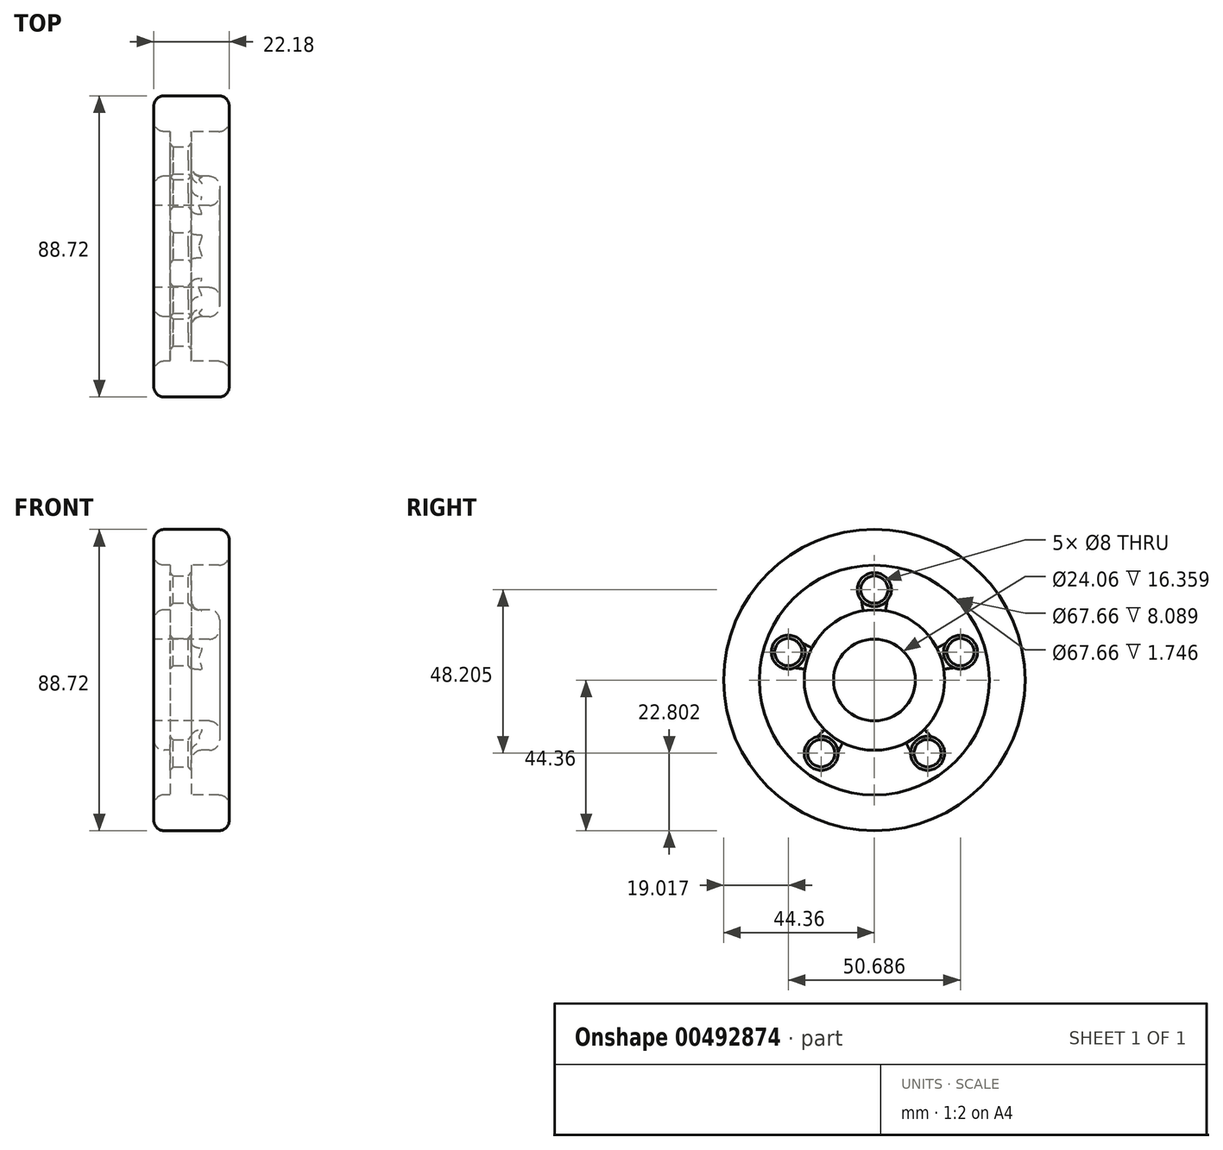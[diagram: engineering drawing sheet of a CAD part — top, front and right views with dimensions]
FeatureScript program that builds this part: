
annotation { "Feature Type Name" : "Feature", "Feature Type Description" : "" }
export const myFeature = defineFeature(function(context is Context, id is Id, definition is map)
    precondition{}
    {
        {
            var Q0;
            Q0=qCreatedBy(makeId("Front.planeOp"),FACE);
            var sketch = newSketch(context, id + "F0", { "sketchPlane" : qUnion([Q0])});
            skLineSegment(sketch, "E0", {"start": v(0, 12.03) * mm, "end": v(19.36, 12.03) * mm});
            skLineSegment(sketch, "E1", {"start": v(19.36, 12.03) * mm, "end": v(19.36, 20.67) * mm});
            skLineSegment(sketch, "E2", {"start": v(19.36, 20.67) * mm, "end": v(11.09, 20.67) * mm});
            skLineSegment(sketch, "E3", {"start": v(11.09, 20.67) * mm, "end": v(11.09, 33.83) * mm});
            skLineSegment(sketch, "E4", {"start": v(11.09, 33.83) * mm, "end": v(22.18, 33.83) * mm});
            skLineSegment(sketch, "E5", {"start": v(22.18, 33.83) * mm, "end": v(22.18, 44.36) * mm});
            skLineSegment(sketch, "E6", {"start": v(22.18, 44.36) * mm, "end": v(0, 44.36) * mm});
            skLineSegment(sketch, "E7", {"start": v(0, 44.36) * mm, "end": v(0, 33.83) * mm});
            skLineSegment(sketch, "E8", {"start": v(0, 33.83) * mm, "end": v(4.75, 33.83) * mm});
            skLineSegment(sketch, "E9", {"start": v(4.75, 33.83) * mm, "end": v(4.75, 20.67) * mm});
            skLineSegment(sketch, "E10", {"start": v(4.75, 20.67) * mm, "end": v(0, 20.67) * mm});
            skLineSegment(sketch, "E11", {"start": v(0, 20.67) * mm, "end": v(0, 12.03) * mm});
            skLineSegment(sketch, "E12", {"start": v(0, 0) * mm, "end": v(19.36, 0) * mm});
            skSolve(sketch);
        }
        {
            var Q0;
            Q0 = qSketchRegion(id + "F0", true);
            var Q1;
            Q1=sQuery(id+"F0.wireOp",EDGE,"E12");
            revolve(context, id + "F1", {"entities" : qUnion([Q0]), "axis" : qUnion([Q1]), "revolveType" : RevolveType.FULL});
        }
        {
            var Q0;
            Q0=makeQuery(id+"F1.opRevolve","SWEPT_FACE",FACE,{"disambiguationData":[OSD([sQuery(id+"F0.wireOp",EDGE,"E3")])]});
            var sketch = newSketch(context, id + "F2", { "sketchPlane" : qUnion([Q0])});
            skCircle(sketch, "E13", {"center": v(0, 26.65) * mm, "radius": 4 * mm});
            skCircle(sketch, "E14.1.0", {"center": v(-25.34, 8.23) * mm, "radius": 4 * mm});
            skCircle(sketch, "E14.2.0", {"center": v(-15.66, -21.56) * mm, "radius": 4 * mm});
            skCircle(sketch, "E14.3.0", {"center": v(15.66, -21.56) * mm, "radius": 4 * mm});
            skCircle(sketch, "E14.4.0", {"center": v(25.34, 8.23) * mm, "radius": 4 * mm});
            skPoint(sketch, "E14.center", {"position": v(0, 0) * mm});
            skSolve(sketch);
        }
        {
            var Q0;
            Q0 = qSketchRegion(id + "F2", true);
            extrude(context, id + "F3", {"entities" : qUnion([Q0]), "operationType" : NewBodyOperationType.REMOVE, "oppositeDirection" : true, "depth" : 25 * mm});
        }
        {
            var Q0;
            Q0=makeQuery(id+"F1.opRevolve","SWEPT_FACE",FACE,{"disambiguationData":[OSD([sQuery(id+"F0.wireOp",EDGE,"E6")])]});
            fillet(context, id + "F4", {"entities" : qUnion([Q0]), "radius" : 3 * mm, "tangentPropagation" : true, "allowEdgeOverflow" : false});
        }
        {
            var Q0;
            Q0=makeQuery(id+"F3.boolean.opBoolean","INTERSECT",EDGE,{"derivedFrom":[makeQuery(id+"F1.opRevolve","SWEPT_FACE",FACE,{"disambiguationData":[OSD([sQuery(id+"F0.wireOp",EDGE,"E9")])]}),makeQuery(id+"F3.opExtrude","SWEPT_FACE",FACE,{"disambiguationData":[OSD([sQuery(id+"F2.wireOp",EDGE,"E14.1.0")])]})]});
            var Q1;
            Q1=makeQuery(id+"F3.boolean.opBoolean","INTERSECT",EDGE,{"derivedFrom":[makeQuery(id+"F1.opRevolve","SWEPT_FACE",FACE,{"disambiguationData":[OSD([sQuery(id+"F0.wireOp",EDGE,"E9")])]}),makeQuery(id+"F3.opExtrude","SWEPT_FACE",FACE,{"disambiguationData":[OSD([sQuery(id+"F2.wireOp",EDGE,"E14.2.0")])]})]});
            var Q2;
            Q2=makeQuery(id+"F3.boolean.opBoolean","COPY",FACE,{"derivedFrom":makeQuery(id+"F3.opExtrude","SWEPT_FACE",FACE,{"disambiguationData":[OSD([sQuery(id+"F2.wireOp",EDGE,"E14.3.0")])]})});
            var Q3;
            Q3=makeQuery(id+"F3.boolean.opBoolean","COPY",FACE,{"derivedFrom":makeQuery(id+"F3.opExtrude","SWEPT_FACE",FACE,{"disambiguationData":[OSD([sQuery(id+"F2.wireOp",EDGE,"E14.4.0")])]})});
            var Q4;
            Q4=makeQuery(id+"F3.boolean.opBoolean","COPY",FACE,{"derivedFrom":makeQuery(id+"F3.opExtrude","SWEPT_FACE",FACE,{"disambiguationData":[OSD([sQuery(id+"F2.wireOp",EDGE,"E13")])]})});
            var Q5;
            Q5=makeQuery(id+"F3.boolean.opBoolean","COPY",FACE,{"derivedFrom":makeQuery(id+"F3.opExtrude","SWEPT_FACE",FACE,{"disambiguationData":[OSD([sQuery(id+"F2.wireOp",EDGE,"E14.2.0")])]})});
            var Q6;
            Q6=makeQuery(id+"F3.boolean.opBoolean","COPY",FACE,{"derivedFrom":makeQuery(id+"F3.opExtrude","SWEPT_FACE",FACE,{"disambiguationData":[OSD([sQuery(id+"F2.wireOp",EDGE,"E14.1.0")])]})});
            chamfer(context, id + "F5", {"entities" : qUnion([Q0, Q1, Q2, Q3, Q4, Q5, Q6]), "width" : 1 * mm, "tangentPropagation" : true});
        }
        {
            var Q0;
            Q0=makeQuery(id+"F1.opRevolve","SWEPT_EDGE",EDGE,{"disambiguationData":[OSD([sQuery(id+"F0.wireOp",EDGE,"E7"),sQuery(id+"F0.wireOp",EDGE,"E8")])]});
            var Q1;
            Q1=makeQuery(id+"F1.opRevolve","SWEPT_EDGE",EDGE,{"disambiguationData":[OSD([sQuery(id+"F0.wireOp",EDGE,"E4"),sQuery(id+"F0.wireOp",EDGE,"E5")])]});
            fillet(context, id + "F6", {"entities" : qUnion([Q0, Q1]), "radius" : 3 * mm, "tangentPropagation" : true, "allowEdgeOverflow" : false});
        }
        {
            var Q0;
            Q0=makeQuery(id+"F1.opRevolve","SWEPT_EDGE",EDGE,{"disambiguationData":[OSD([sQuery(id+"F0.wireOp",EDGE,"E10"),sQuery(id+"F0.wireOp",EDGE,"E11")])]});
            var Q1;
            Q1=makeQuery(id+"F1.opRevolve","SWEPT_FACE",FACE,{"disambiguationData":[OSD([sQuery(id+"F0.wireOp",EDGE,"E1")])]});
            var Q2;
            Q2=makeQuery(id+"F1.opRevolve","SWEPT_FACE",FACE,{"disambiguationData":[OSD([sQuery(id+"F0.wireOp",EDGE,"E2")])]});
            fillet(context, id + "F7", {"entities" : qUnion([Q0, Q1, Q2]), "radius" : 3 * mm, "tangentPropagation" : true, "allowEdgeOverflow" : false});
        }
    });
